# Revit family: Kamstrup_Multical_21
name_source: partatom
category: Арматура трубопроводов
revit_build: Autodesk Revit 2016 (Build: 20150714_1515(x64)
units: mm (PartAtom-declared; Revit-internal decimal feet)

## family parameters
Всегда вертикально = Да
На основе рабочей плоскости = Нет
Общий = Нет
При загрузке вырезать с полостями = Нет
Размер круглого соединителя = Использовать диаметр
Тип детали = Встроенный датчик

## types (5) — shared parameters
A = 10 мм
ID01 = 7 Счетчик горячей воды
ID02 = 8 Счетчик холодной воды
URL = https://www.kamstrup.com
Адрес = 141008, Московская обл., г. Мытищи, ул. Колпакова, 26
Изготовитель = ЗАО «Камструп»
Телефон = +7 495 545 00 01

## per-type parameters (varying)
| type | DN | G | L | Тип1 | Тип2 |
| 021-66-A0A | 15 мм | 20 мм | 110 мм | Multical 021-66-A0A7 | Multical 021-66-A0A8 |
| 021-66-A0D | 15 мм | 20 мм | 110 мм | Multical 021-66-A0D7 | Multical 021-66-A0D8 |
| 021-66-A0G | 20 мм | 25 мм | 105 мм | Multical 021-66-A0G7 | Multical 021-66-A0G8 |
| 021-66-A0H | 20 мм | 25 мм | 130 мм | Multical 021-66-A0H7 | Multical 021-66-A0H8 |
| 021-66-A0L | 20 мм | 25 мм | 130 мм | Multical 021-66-A0L7 | Multical 021-66-A0L8 |
